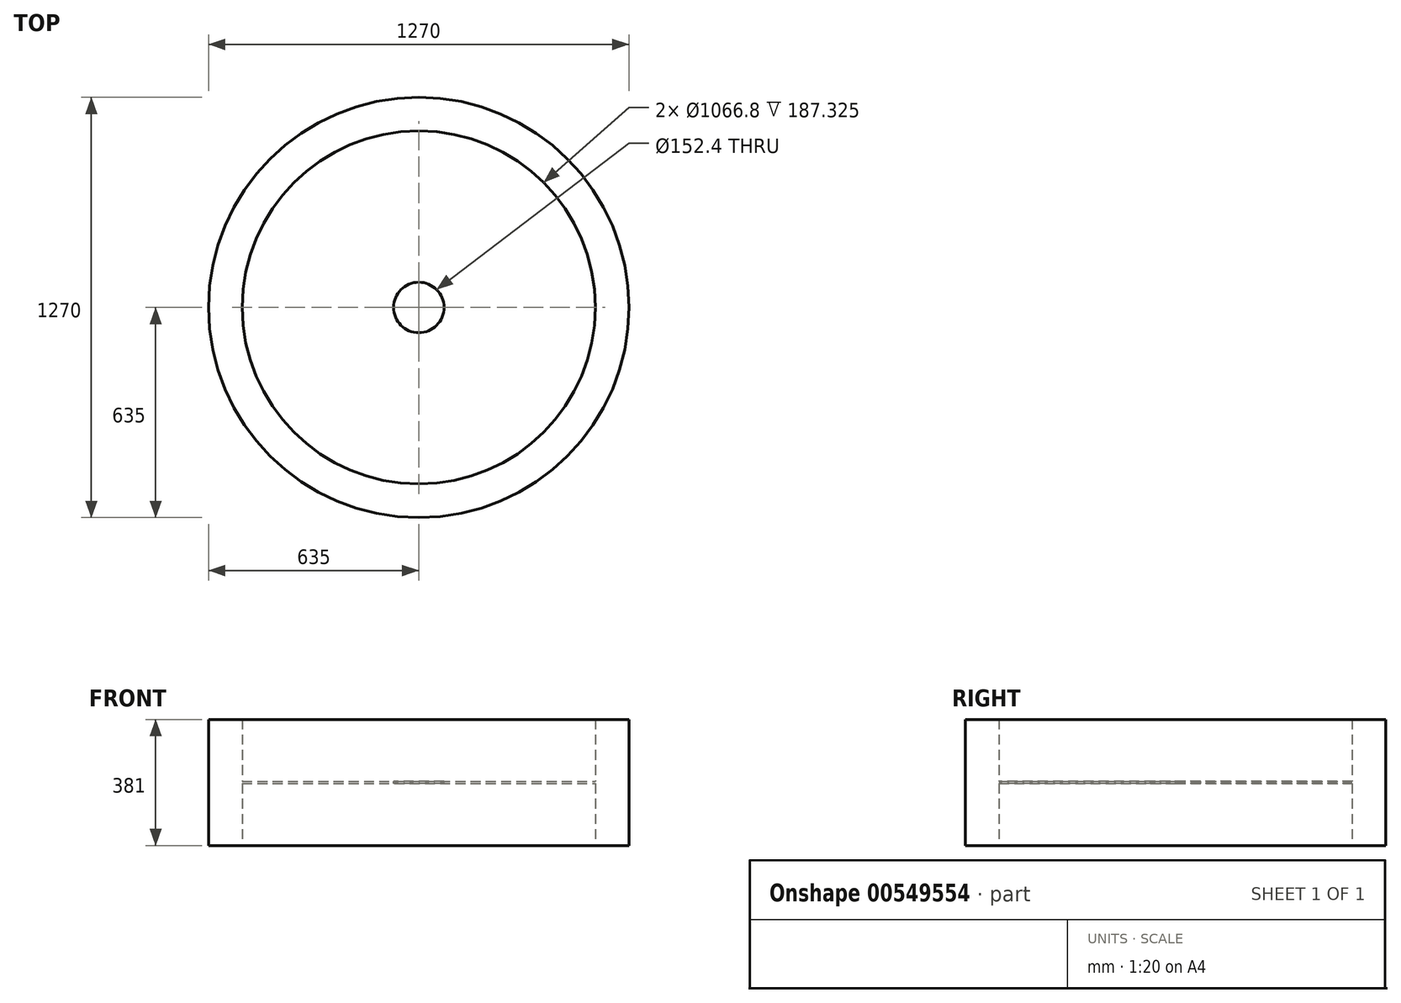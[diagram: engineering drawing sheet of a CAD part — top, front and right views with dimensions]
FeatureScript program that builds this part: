
annotation { "Feature Type Name" : "Feature", "Feature Type Description" : "" }
export const myFeature = defineFeature(function(context is Context, id is Id, definition is map)
    precondition{}
    {
        {
            var Q0;
            Q0=qCreatedBy(makeId("Front.planeOp"),FACE);
            var sketch = newSketch(context, id + "F0", { "sketchPlane" : qUnion([Q0])});
            skLineSegment(sketch, "E0", {"start": v(533.4, -3.18) * mm, "end": v(533.4, -190.5) * mm});
            skLineSegment(sketch, "E1", {"start": v(533.4, -190.5) * mm, "end": v(635, -190.5) * mm});
            skLineSegment(sketch, "E2", {"start": v(635, -190.5) * mm, "end": v(635, 190.5) * mm});
            skLineSegment(sketch, "E3", {"start": v(635, 190.5) * mm, "end": v(533.4, 190.5) * mm});
            skLineSegment(sketch, "E4", {"start": v(533.4, 190.5) * mm, "end": v(533.4, 3.18) * mm});
            skLineSegment(sketch, "E5", {"start": v(533.4, 3.18) * mm, "end": v(0, 3.17) * mm});
            skLineSegment(sketch, "E6", {"start": v(0, 3.17) * mm, "end": v(0, 0) * mm});
            skLineSegment(sketch, "E7", {"start": v(533.4, -3.17) * mm, "end": v(0, -3.18) * mm});
            skLineSegment(sketch, "E8", {"start": v(0, -3.17) * mm, "end": v(0, 0) * mm});
            skSolve(sketch);
        }
        {
            var Q0;
            Q0 = qSketchRegion(id + "F0", true);
            var Q1;
            Q1=sQuery(id+"F0.wireOp",EDGE,"E8");
            revolve(context, id + "F1", {"entities" : qUnion([Q0]), "axis" : qUnion([Q1]), "revolveType" : RevolveType.FULL});
        }
        {
            var Q0;
            Q0=makeQuery(id+"F1.opRevolve","SWEPT_FACE",FACE,{"disambiguationData":[OSD([sQuery(id+"F0.wireOp",EDGE,"E5")])]});
            var sketch = newSketch(context, id + "F2", { "sketchPlane" : qUnion([Q0])});
            skCircle(sketch, "E9", {"center": v(0, 0) * mm, "radius": 76.2 * mm});
            skSolve(sketch);
        }
        {
            var Q0;
            Q0 = qSketchRegion(id + "F2", true);
            extrude(context, id + "F3", {"entities" : qUnion([Q0]), "operationType" : NewBodyOperationType.REMOVE, "endBound" : BoundingType.UP_TO_NEXT, "oppositeDirection" : true, "depth" : 25.4 * mm, "offsetDistance" : 25.4 * mm});
        }
    });
